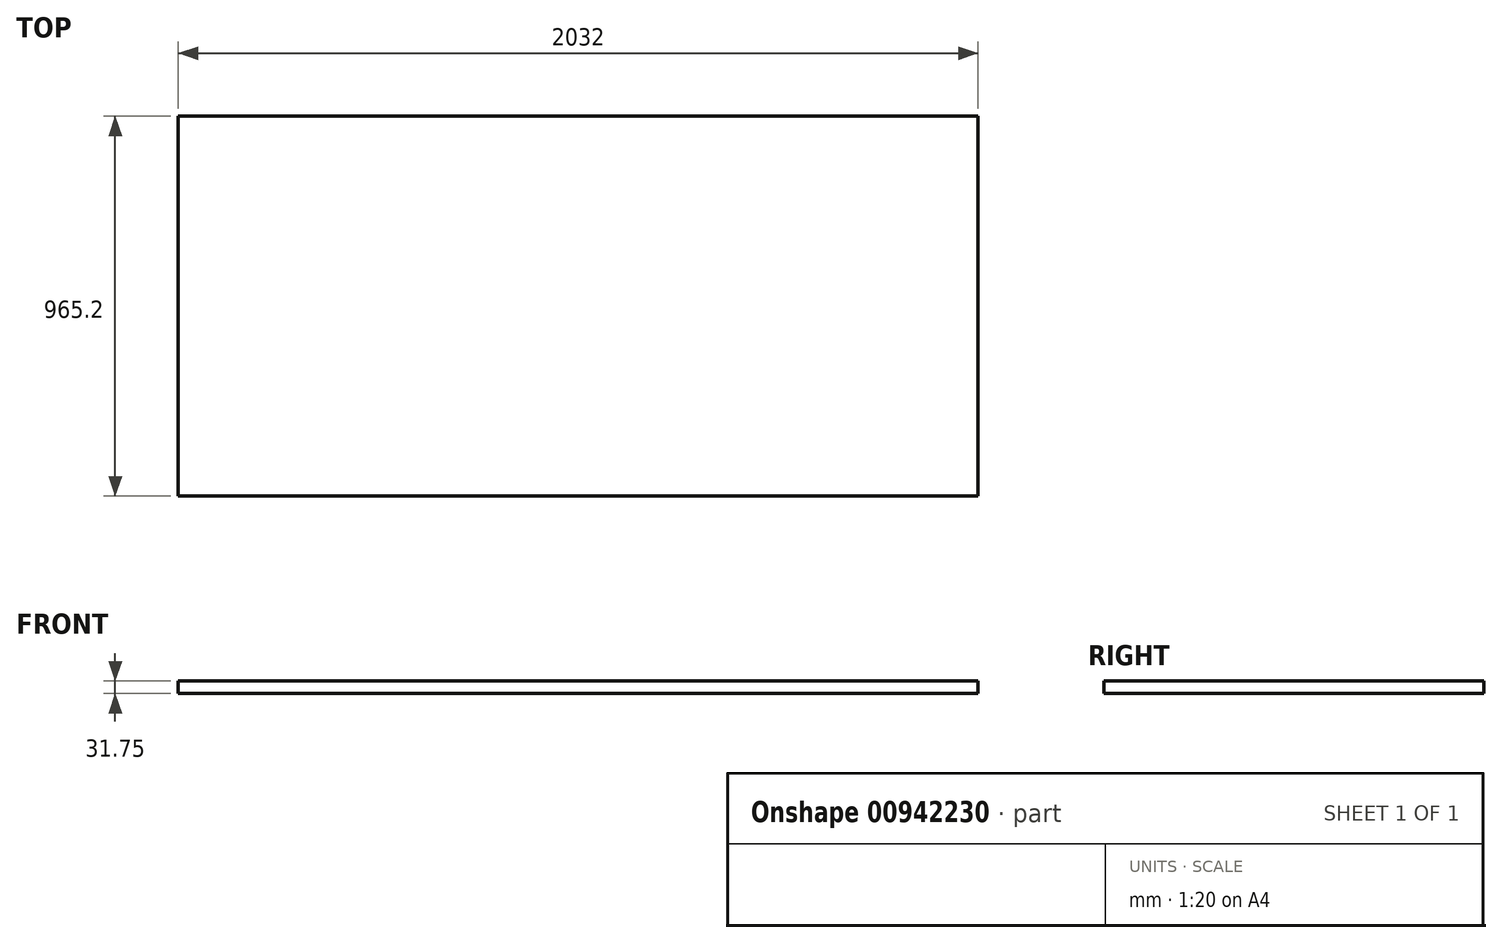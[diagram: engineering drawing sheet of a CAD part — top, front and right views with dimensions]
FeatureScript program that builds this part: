
annotation { "Feature Type Name" : "Feature", "Feature Type Description" : "" }
export const myFeature = defineFeature(function(context is Context, id is Id, definition is map)
    precondition{}
    {
        {
            var Q0;
            Q0=qCreatedBy(makeId("Top.planeOp"),FACE);
            var sketch = newSketch(context, id + "F0", { "sketchPlane" : qUnion([Q0])});
            skLineSegment(sketch, "E0.bottom", {"start": v(1016, 482.6) * mm, "end": v(-1016, 482.6) * mm});
            skLineSegment(sketch, "E0.top", {"start": v(1016, -482.6) * mm, "end": v(-1016, -482.6) * mm});
            skLineSegment(sketch, "E0.left", {"start": v(1016, 482.6) * mm, "end": v(1016, -482.6) * mm});
            skLineSegment(sketch, "E0.right", {"start": v(-1016, 482.6) * mm, "end": v(-1016, -482.6) * mm});
            skPoint(sketch, "E0.middle", {"position": v(0, 0) * mm});
            skSolve(sketch);
        }
        {
            var Q0;
            Q0 = qSketchRegion(id + "F0", true);
            extrude(context, id + "F1", {"entities" : qUnion([Q0]), "depth" : 31.75 * mm, "offsetDistance" : 25.4 * mm});
        }
    });
